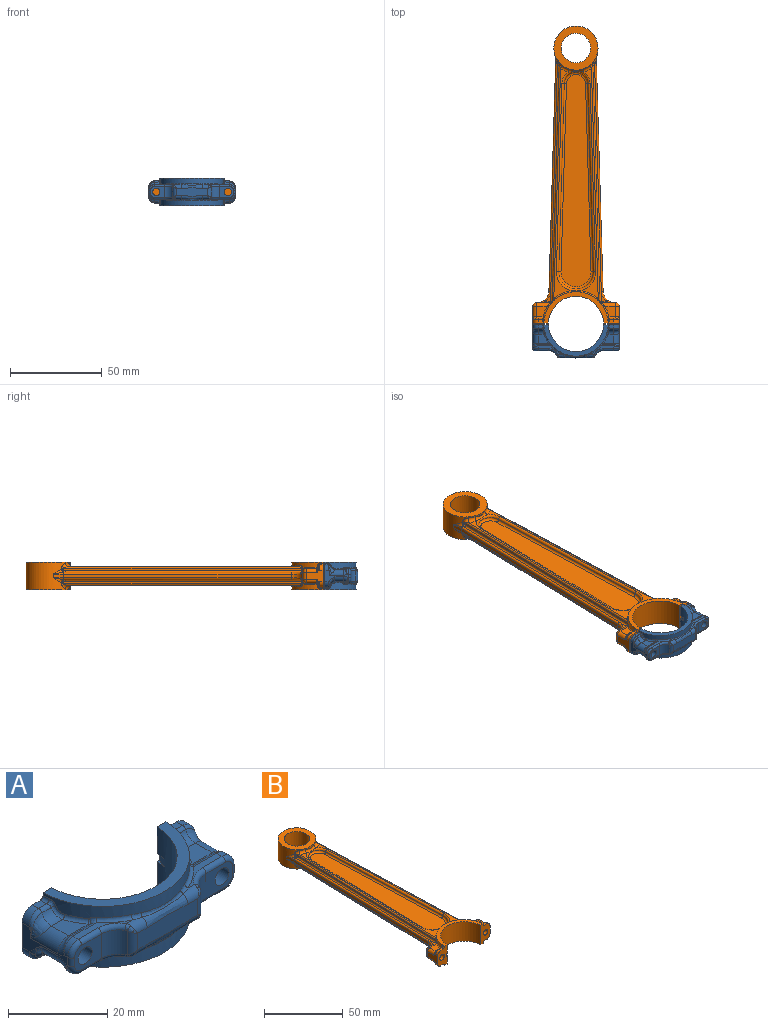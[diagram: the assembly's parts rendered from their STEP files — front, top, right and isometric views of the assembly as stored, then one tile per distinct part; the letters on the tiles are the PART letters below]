
ASSEMBLY  parts=2 mates=1
PART A: 147 faces, bbox 54.2x18.3x15.2 mm
  f0: plane 15.01x8.51mm, normal (0,1,0), area 92.1mm2, adj f1,f27,f28,f29,f30,f38,f39,f40
  f1: cylinder r=15mm len=29.98mm, axis (0,0,-1), area 686.7mm2, adj f0,f36,f38,f39,f144,f145,f146
  f2: plane 12.58x4.23mm, normal (0,0,-1), area 11.7mm2, adj f8,f50,f58,f77,f78,f120
  f3: plane 12.58x4.52mm, normal (0,0,1), area 13.7mm2, adj f16,f54,f61,f66,f67,f137
  f4: cylinder r=3mm len=4.6mm, axis (0,-1,0), area 21.7mm2, adj f5,f19,f21,f92
  f5: torus R=3.9mm, axis (1,0,0), area 8.1mm2, adj f4,f19,f22,f52
  f6: cylinder r=3mm len=3mm, axis (0,-1,0), area 4mm2, adj f19,f23,f52,f70
  f7: torus R=3.9mm, axis (-1,0,0), area 8.1mm2, adj f9,f24,f28,f51
  f8: cylinder r=3mm len=3mm, axis (0,1,0), area 4mm2, adj f2,f28,f51,f79
  f9: cylinder r=3mm len=4.6mm, axis (0,1,0), area 21.7mm2, adj f7,f25,f28,f86
  f10: cylinder r=3mm len=7.69mm, axis (0,-1,0), area 27.1mm2, adj f11,f28,f31,f89,f90
  f11: torus R=3.9mm, axis (-1,0,0), area 5.6mm2, adj f10,f28,f32,f49
  f12: cylinder r=3mm len=3mm, axis (0,-1,0), area 5.7mm2, adj f28,f33,f49,f81
  f13: plane 7.59x6mm, normal (0,-1,0), area 31.3mm2, adj f29,f47,f78,f79,f80,f81,f82
  f14: plane 17.15x4.54mm, normal (0,-1,0), area 71.8mm2, adj f56,f57,f58,f59,f60,f61,f62,f63
  f15: plane 7.59x6mm, normal (0,-1,0), area 31.3mm2, adj f20,f46,f67,f68,f69,f70,f71
  f16: cylinder r=3mm len=3mm, axis (0,1,0), area 5.7mm2, adj f3,f19,f55,f68
  f17: torus R=3.9mm, axis (1,0,0), area 5.6mm2, adj f18,f19,f34,f55
  f18: cylinder r=3mm len=7.69mm, axis (0,1,0), area 27.1mm2, adj f17,f19,f35,f94,f95
  f19: plane 13.22x6.22mm, normal (-1,0,0), area 25.3mm2, adj f4,f5,f6,f16,f17,f18,f36,f44
  f20: cylinder r=2mm len=14mm, axis (0,-1,0), area 175.9mm2, adj f15,f36
  f21: plane 5.58x4.6mm, normal (0,0,-1), area 19.6mm2, adj f4,f22,f91,f113
  f22: cylinder r=0.9mm len=5.64mm, axis (1,0,0), area 5.4mm2, adj f5,f21,f53,f114
  f23: plane 12.58x4.23mm, normal (0,0,-1), area 11.7mm2, adj f6,f53,f62,f71,f72,f116
  f24: cylinder r=0.9mm len=5.64mm, axis (1,0,0), area 5.4mm2, adj f7,f25,f50,f122
  f25: plane 5.58x4.6mm, normal (0,0,-1), area 19.6mm2, adj f9,f24,f87,f123
  f26: plane 2.32x1.63mm, normal (0,0,-1), area 3.7mm2, adj f36,f45,f102,f110
  f27: plane 2.32x1.63mm, normal (0,0,-1), area 3.7mm2, adj f0,f43,f109,f126
  f28: plane 13.22x6.22mm, normal (1,0,0), area 25.3mm2, adj f0,f7,f8,f9,f10,f11,f12,f42
  f29: cylinder r=2mm len=14mm, axis (0,-1,0), area 175.9mm2, adj f0,f13
  f30: plane 2.33x1.75mm, normal (0,0,1), area 3.9mm2, adj f0,f42,f106,f127
  f31: plane 5.64x4.74mm, normal (0,0,1), area 20.2mm2, adj f10,f32,f88,f130
  f32: cylinder r=0.9mm len=5.69mm, axis (-1,0,0), area 3.8mm2, adj f11,f31,f48,f131
  f33: plane 12.58x4.52mm, normal (0,0,1), area 13.7mm2, adj f12,f48,f57,f82,f83,f133
  f34: cylinder r=0.9mm len=5.69mm, axis (-1,0,0), area 3.8mm2, adj f17,f35,f54,f139
  f35: plane 5.64x4.74mm, normal (0,0,1), area 20.2mm2, adj f18,f34,f93,f140
  f36: plane 15.01x8.51mm, normal (0,1,0), area 93.4mm2, adj f1,f19,f20,f26,f37,f38,f39,f40
  f37: plane 2.33x1.75mm, normal (0,0,1), area 3.9mm2, adj f36,f44,f99,f143
  f38: plane 34.99x17mm, normal (0,0,1), area 125.1mm2, adj f0,f1,f36,f40
  f39: plane 34.99x17mm, normal (0,0,-1), area 125.1mm2, adj f0,f1,f36,f41
  f40: cylinder r=17.5mm len=34.99mm, axis (0,0,-1), area 143.5mm2, adj f0,f36,f38,f127,f128,f129,f130,f131
  f41: cylinder r=17.5mm len=34.99mm, axis (0,0,-1), area 151.4mm2, adj f0,f36,f39,f110,f111,f112,f113,f114
  f42: cylinder r=3mm len=3mm, axis (0,1,0), area 9.2mm2, adj f0,f28,f30,f105
  f43: cylinder r=3mm len=3mm, axis (0,-1,0), area 9.2mm2, adj f0,f27,f28,f108
  f44: cylinder r=3mm len=3mm, axis (0,1,0), area 9.2mm2, adj f19,f36,f37,f98
  f45: cylinder r=3mm len=3mm, axis (0,-1,0), area 9.2mm2, adj f19,f26,f36,f101
  f46: cylinder r=5mm len=6mm, axis (0,0,1), area 33.8mm2, adj f15,f63,f65,f66,f72,f73
  f47: cylinder r=5mm len=6mm, axis (0,0,-1), area 33.8mm2, adj f13,f56,f76,f77,f83,f84
  f48: cylinder r=1mm len=6.66mm, axis (-1,0,0), area 4.6mm2, adj f32,f33,f49,f132
  f49: bspline ~3.51x3mm, area 1.4mm2, adj f11,f12,f48
  f50: cylinder r=1mm len=6.92mm, axis (1,0,0), area 6.8mm2, adj f2,f24,f51,f121
  f51: bspline ~3x3mm, area 2mm2, adj f7,f8,f50
  f52: bspline ~3.67x3mm, area 2mm2, adj f5,f6,f53
  f53: cylinder r=1mm len=6.92mm, axis (1,0,0), area 6.8mm2, adj f22,f23,f52,f115
  f54: cylinder r=1mm len=6.66mm, axis (-1,0,0), area 4.6mm2, adj f3,f34,f55,f138
  f55: bspline ~3.51x3mm, area 1.4mm2, adj f16,f17,f54
  f56: cylinder r=2mm len=5.81mm, axis (0,0,-1), area 11.1mm2, adj f14,f47,f75,f85
  f57: cylinder r=2mm len=3.87mm, axis (-1,0,0), area 9.9mm2, adj f14,f33,f59,f84,f85,f134
  f58: cylinder r=2mm len=3.87mm, axis (1,0,0), area 9.9mm2, adj f2,f14,f60,f75,f76,f119
  f59: bspline ~12.87x2.37mm, area 22.9mm2, adj f14,f57,f61,f135
  f60: bspline ~12.87x2.37mm, area 22.9mm2, adj f14,f58,f62,f118
  f61: cylinder r=2mm len=3.87mm, axis (-1,0,0), area 9.9mm2, adj f3,f14,f59,f64,f65,f136
  f62: cylinder r=2mm len=3.87mm, axis (1,0,0), area 9.9mm2, adj f14,f23,f60,f73,f74,f117
  f63: cylinder r=2mm len=5.81mm, axis (0,0,1), area 11.1mm2, adj f14,f46,f64,f74
  f64: bspline ~1.87x1.87mm, area 1.2mm2, adj f61,f63,f65
  f65: bspline ~1.8x1.41mm, area 1mm2, adj f46,f61,f64,f66
  f66: torus R=6mm, axis (0,0,1), area 8.8mm2, adj f3,f46,f65,f67
  f67: cylinder r=1mm len=5.59mm, axis (-1,0,0), area 8.8mm2, adj f3,f15,f66,f68
  f68: torus R=2mm, axis (0,1,0), area 6.5mm2, adj f15,f16,f67,f69
  f69: cylinder r=1mm len=2mm, axis (0,0,-1), area 3.1mm2, adj f15,f19,f68,f70
  f70: torus R=2mm, axis (0,1,0), area 6.5mm2, adj f6,f15,f69,f71
  f71: cylinder r=1mm len=5.59mm, axis (1,0,0), area 8.8mm2, adj f15,f23,f70,f72
  f72: torus R=6mm, axis (0,0,1), area 8.8mm2, adj f23,f46,f71,f73
  f73: bspline ~2.01x1.47mm, area 1mm2, adj f46,f62,f72,f74
  f74: bspline ~1.87x1.87mm, area 1.2mm2, adj f62,f63,f73
  f75: bspline ~1.87x1.87mm, area 1.2mm2, adj f56,f58,f76
  f76: bspline ~1.8x1.41mm, area 1mm2, adj f47,f58,f75,f77
  f77: torus R=6mm, axis (0,0,1), area 8.8mm2, adj f2,f47,f76,f78
  f78: cylinder r=1mm len=5.59mm, axis (1,0,0), area 8.8mm2, adj f2,f13,f77,f79
  f79: torus R=2mm, axis (0,1,0), area 6.5mm2, adj f8,f13,f78,f80
  f80: cylinder r=1mm len=2mm, axis (0,0,-1), area 3.1mm2, adj f13,f28,f79,f81
  f81: torus R=2mm, axis (0,1,0), area 6.5mm2, adj f12,f13,f80,f82
  f82: cylinder r=1mm len=5.59mm, axis (-1,0,0), area 8.8mm2, adj f13,f33,f81,f83
  f83: torus R=6mm, axis (0,0,1), area 8.8mm2, adj f33,f47,f82,f84
  f84: bspline ~2.01x1.47mm, area 1mm2, adj f47,f57,f83,f85
  f85: bspline ~1.87x1.87mm, area 1.2mm2, adj f56,f57,f84
  f86: torus R=6mm, axis (0,-1,0), area 11.5mm2, adj f9,f87,f107,f108
  f87: cylinder r=3mm len=3.2mm, axis (-1,0,0), area 11.5mm2, adj f25,f86,f109,f124
  f88: cylinder r=3mm len=3.19mm, axis (-1,0,0), area 10.3mm2, adj f31,f89,f106,f129
  f89: bspline ~4.43x3.56mm, area 10.6mm2, adj f10,f88,f90,f104,f105
  f90: bspline ~3.15x2.14mm, area 1.2mm2, adj f10,f89,f103
  f91: cylinder r=3mm len=3.2mm, axis (1,0,0), area 11.5mm2, adj f21,f92,f102,f112
  f92: torus R=6mm, axis (0,1,0), area 11.5mm2, adj f4,f91,f100,f101
  f93: cylinder r=3mm len=3.19mm, axis (1,0,0), area 10.3mm2, adj f35,f94,f99,f141
  f94: bspline ~4.44x3.7mm, area 10.6mm2, adj f18,f93,f95,f97,f98
  f95: bspline ~3.15x2.14mm, area 1.2mm2, adj f18,f94,f96
  f96: bspline ~2.53x0.55mm, area 0.4mm2, adj f19,f95,f97
  f97: bspline ~0.67x0.67mm, area 0.2mm2, adj f19,f94,f96,f98
  f98: bspline ~3.39x3.32mm, area 4.5mm2, adj f44,f94,f97,f99
  f99: cylinder r=1mm len=2.62mm, axis (1,0,0), area 2.9mm2, adj f37,f93,f98,f142
  f100: bspline ~3.73x3.37mm, area 1.9mm2, adj f19,f92,f101
  f101: bspline ~3.72x3.37mm, area 5.2mm2, adj f45,f92,f100,f102
  f102: cylinder r=1mm len=2.61mm, axis (1,0,0), area 3.2mm2, adj f26,f91,f101,f111
  f103: bspline ~2.38x0.52mm, area 0.4mm2, adj f28,f90,f104
  f104: bspline ~0.65x0.62mm, area 0.2mm2, adj f28,f89,f103,f105
  f105: bspline ~3.39x3.32mm, area 4.5mm2, adj f42,f89,f104,f106
  f106: cylinder r=1mm len=2.62mm, axis (-1,0,0), area 2.9mm2, adj f30,f88,f105,f128
  f107: bspline ~3.73x3.37mm, area 1.9mm2, adj f28,f86,f108
  f108: bspline ~3.72x3.37mm, area 5.2mm2, adj f43,f86,f107,f109
  f109: cylinder r=1mm len=2.61mm, axis (-1,0,0), area 3.2mm2, adj f27,f87,f108,f125
  f110: torus R=18.3mm, axis (0,0,1), area 2mm2, adj f26,f36,f41,f111
  f111: bspline ~2.11x1.77mm, area 2mm2, adj f41,f102,f110,f112
  f112: bspline ~3.71x2.95mm, area 4.1mm2, adj f41,f91,f111,f113
  f113: torus R=18.3mm, axis (0,0,1), area 6.3mm2, adj f21,f41,f112,f114
  f114: bspline ~1.55x1.48mm, area 1mm2, adj f22,f41,f113,f115
  f115: bspline ~2.39x2.39mm, area 2.6mm2, adj f41,f53,f114,f116
  f116: torus R=18.3mm, axis (0,0,1), area 8.7mm2, adj f23,f41,f115,f117
  f117: bspline ~4.41x1.85mm, area 2.4mm2, adj f41,f62,f116,f118
  f118: bspline ~13.52x1.54mm, area 9.3mm2, adj f41,f60,f117,f119
  f119: bspline ~4.92x2.11mm, area 2.4mm2, adj f41,f58,f118,f120
  f120: torus R=18.3mm, axis (0,0,1), area 8.7mm2, adj f2,f41,f119,f121
  f121: bspline ~2.39x2.39mm, area 2.6mm2, adj f41,f50,f120,f122
  f122: bspline ~1.55x1.48mm, area 1mm2, adj f24,f41,f121,f123
  f123: torus R=18.3mm, axis (0,0,1), area 6.3mm2, adj f25,f41,f122,f124
  f124: bspline ~3.71x2.95mm, area 4.1mm2, adj f41,f87,f123,f125
  f125: bspline ~2.11x1.77mm, area 2mm2, adj f41,f109,f124,f126
  f126: torus R=18.3mm, axis (0,0,1), area 2mm2, adj f0,f27,f41,f125
  f127: torus R=18.3mm, axis (0,0,1), area 2.1mm2, adj f0,f30,f40,f128
  f128: bspline ~2.01x1.48mm, area 1.8mm2, adj f40,f106,f127,f129
  f129: bspline ~3.68x2.66mm, area 3.7mm2, adj f40,f88,f128,f130
  f130: torus R=18.3mm, axis (0,0,1), area 6.5mm2, adj f31,f40,f129,f131
  f131: bspline ~1.35x1.31mm, area 0.6mm2, adj f32,f40,f130,f132
  f132: bspline ~2.17x2.13mm, area 1.8mm2, adj f40,f48,f131,f133
  f133: torus R=18.3mm, axis (0,0,1), area 9.2mm2, adj f33,f40,f132,f134
  f134: bspline ~4.92x2.11mm, area 2.4mm2, adj f40,f57,f133,f135
  f135: bspline ~13.52x1.54mm, area 9.3mm2, adj f40,f59,f134,f136
  f136: bspline ~4.41x1.85mm, area 2.4mm2, adj f40,f61,f135,f137
  f137: torus R=18.3mm, axis (0,0,1), area 9.2mm2, adj f3,f40,f136,f138
  f138: bspline ~2.17x2.13mm, area 1.8mm2, adj f40,f54,f137,f139
  f139: bspline ~1.35x1.31mm, area 0.6mm2, adj f34,f40,f138,f140
  f140: torus R=18.3mm, axis (0,0,1), area 6.5mm2, adj f35,f40,f139,f141
  f141: bspline ~3.68x2.66mm, area 3.7mm2, adj f40,f93,f140,f142
  f142: bspline ~2.08x1.64mm, area 1.8mm2, adj f40,f99,f141,f143
  f143: torus R=18.3mm, axis (0,0,1), area 2.1mm2, adj f36,f37,f40,f142
  f144: plane 2.57x2mm, normal (-0.94,0.34,0), area 5.5mm2, adj f0,f1,f145,f146
  f145: plane 2.57x0.94mm, normal (0,0,1), area 0.7mm2, adj f0,f1,f144
  f146: plane 2.57x0.94mm, normal (0,0,-1), area 0.7mm2, adj f0,f1,f144
PART B: 228 faces, bbox 50.3x161.5x16.2 mm
  f0: cylinder r=15mm len=29.98mm, axis (0,0,-1), area 686.7mm2, adj f1,f18,f19,f41,f225,f226,f227
  f1: plane 15.01x8.51mm, normal (0,-1,0), area 92.1mm2, adj f0,f16,f17,f18,f19,f42,f44,f47
  f2: cylinder r=0.8mm len=1.2mm, axis (0,0,-1), area 0.7mm2, adj f12,f16,f37,f103
  f3: cylinder r=0.8mm len=1.2mm, axis (0,0,-1), area 0.7mm2, adj f11,f16,f38,f108
  f4: cylinder r=0.8mm len=1.2mm, axis (0,0,-1), area 0.7mm2, adj f8,f17,f35,f96
  f5: cylinder r=0.8mm len=1.2mm, axis (0,0,-1), area 0.7mm2, adj f7,f17,f36,f101
  f6: cylinder r=2mm len=7.78mm, axis (-1,0,0), area 18.6mm2, adj f24,f40,f59,f127,f128,f129,f133
  f7: bspline ~0.51x0.32mm, area 0mm2, adj f5,f17,f69,f130
  f8: bspline ~0.51x0.24mm, area 0mm2, adj f4,f17,f68,f162
  f9: cylinder r=2mm len=7.78mm, axis (-1,0,0), area 18.6mm2, adj f26,f43,f64,f159,f160,f161,f163
  f10: cylinder r=2mm len=7.78mm, axis (1,0,0), area 18.6mm2, adj f27,f43,f67,f143,f144,f145,f149
  f11: bspline ~0.51x0.32mm, area 0mm2, adj f3,f16,f71,f146
  f12: bspline ~0.51x0.24mm, area 0mm2, adj f2,f16,f70,f114
  f13: cylinder r=2mm len=7.78mm, axis (1,0,0), area 18.6mm2, adj f25,f40,f62,f111,f112,f113,f115
  f14: plane 125.27x9.35mm, normal (0,0,1), area 160.3mm2, adj f23,f82,f85,f106,f107,f216
  f15: plane 125.27x9.35mm, normal (0,0,-1), area 160.3mm2, adj f22,f76,f79,f99,f100,f203
  f16: cylinder r=17.5mm len=34.99mm, axis (0,0,-1), area 109.5mm2, adj f1,f2,f3,f11,f12,f19,f41,f103
  f17: cylinder r=17.5mm len=34.99mm, axis (0,0,-1), area 109.5mm2, adj f1,f4,f5,f7,f8,f18,f41,f96
  f18: plane 34.99x17mm, normal (0,0,-1), area 125.1mm2, adj f0,f1,f17,f41
  f19: plane 34.99x17mm, normal (0,0,1), area 125.1mm2, adj f0,f1,f16,f41
  f20: plane 125.27x9.35mm, normal (0,0,-1), area 160.3mm2, adj f22,f79,f80,f95,f97,f201
  f21: plane 125.27x9.35mm, normal (0,0,1), area 160.3mm2, adj f23,f81,f82,f102,f104,f218
  f22: torus R=7.67mm, axis (0,0,1), area 36mm2, adj f15,f20,f75,f76,f80,f202
  f23: torus R=7.67mm, axis (0,0,1), area 36mm2, adj f14,f21,f81,f85,f86,f217
  f24: plane 5.85x5.7mm, normal (0,0,-1), area 25.9mm2, adj f6,f58,f135,f136
  f25: plane 5.85x5.7mm, normal (0,0,1), area 25.9mm2, adj f13,f61,f118,f119
  f26: plane 5.85x5.7mm, normal (0,0,-1), area 25.9mm2, adj f9,f63,f166,f167
  f27: plane 5.85x5.7mm, normal (0,0,1), area 25.9mm2, adj f10,f65,f151,f152
  f28: plane 5.6x2.76mm, normal (0,0,1), area 4.4mm2, adj f70,f112,f182
  f29: plane 5.6x2.76mm, normal (0,0,1), area 4.4mm2, adj f71,f144,f192
  f30: plane 5.6x2.76mm, normal (0,0,-1), area 4.4mm2, adj f69,f128,f177
  f31: plane 5.6x2.76mm, normal (0,0,-1), area 4.4mm2, adj f68,f160,f187
  f32: plane 123.76x3.64mm, normal (-1,0.03,0), area 247.6mm2, adj f53,f110,f186,f193
  f33: plane 123.76x3.64mm, normal (1,0.03,0), area 247.6mm2, adj f52,f109,f178,f181
  f34: cylinder r=12mm len=24mm, axis (0,0,-1), area 794.7mm2, adj f88,f89,f109,f110,f195,f196,f199,f200
  f35: plane 129.39x3.8mm, normal (-1,0.03,0), area 155.3mm2, adj f4,f68,f95,f197,f199
  f36: plane 129.39x3.8mm, normal (1,0.03,0), area 155.3mm2, adj f5,f69,f99,f205,f207
  f37: plane 129.39x3.8mm, normal (1,0.03,0), area 155.3mm2, adj f2,f70,f102,f220,f221
  f38: plane 129.39x3.8mm, normal (-1,0.03,0), area 155.3mm2, adj f3,f71,f106,f211,f214
  f39: plane 9x6mm, normal (1,0,0), area 41.5mm2, adj f41,f58,f60,f61,f91,f92,f117,f131
  f40: plane 4x0.25mm, normal (0,1,0), area 1mm2, adj f6,f13,f52,f60
  f41: plane 15.01x8.51mm, normal (0,-1,0), area 93.4mm2, adj f0,f16,f17,f18,f19,f39,f48,f51
  f42: plane 9x6mm, normal (-1,0,0), area 41.5mm2, adj f1,f63,f65,f66,f93,f94,f147,f165
  f43: plane 4x0.25mm, normal (0,1,0), area 1mm2, adj f9,f10,f53,f66
  f44: plane 2.33x1.7mm, normal (0,0,1), area 3.8mm2, adj f1,f94,f155,f158
  f45: plane 3.88x0.41mm, normal (0,1,0), area 1.4mm2, adj f148,f151,f153,f155,f156
  f46: plane 3.88x0.41mm, normal (0,1,0), area 1.4mm2, adj f164,f167,f170,f171,f172
  f47: plane 2.33x1.7mm, normal (0,0,-1), area 3.8mm2, adj f1,f93,f172,f174
  f48: plane 2.33x1.7mm, normal (0,0,1), area 3.8mm2, adj f41,f91,f124,f126
  f49: plane 3.88x0.41mm, normal (0,1,0), area 1.4mm2, adj f116,f119,f122,f123,f124
  f50: plane 3.88x0.41mm, normal (0,1,0), area 1.4mm2, adj f132,f135,f137,f139,f140
  f51: plane 2.33x1.7mm, normal (0,0,-1), area 3.8mm2, adj f41,f92,f139,f142
  f52: cylinder r=6.5mm len=6.5mm, axis (0,0,-1), area 24.3mm2, adj f33,f40,f175,f176,f177,f182,f183,f184
  f53: cylinder r=6.5mm len=6.5mm, axis (0,0,1), area 24.3mm2, adj f32,f43,f187,f188,f189,f190,f191,f192
  f54: plane 4x4mm, normal (0,-1,0), area 12.6mm2, adj f55
  f55: cylinder r=2mm len=9mm, axis (0,-1,0), area 113.1mm2, adj f1,f54
  f56: plane 4x4mm, normal (0,-1,0), area 12.6mm2, adj f57
  f57: cylinder r=2mm len=9mm, axis (0,-1,0), area 113.1mm2, adj f41,f56
  f58: cylinder r=2mm len=5.7mm, axis (0,1,0), area 17.9mm2, adj f24,f39,f59,f132
  f59: sphere r=2mm, area 4mm2, adj f6,f58,f60
  f60: cylinder r=2mm len=4mm, axis (0,0,-1), area 12.6mm2, adj f39,f40,f59,f62
  f61: cylinder r=2mm len=5.7mm, axis (0,-1,0), area 17.9mm2, adj f25,f39,f62,f116
  f62: sphere r=2mm, area 4mm2, adj f13,f60,f61
  f63: cylinder r=2mm len=5.7mm, axis (0,-1,0), area 17.9mm2, adj f26,f42,f64,f164
  f64: sphere r=2mm, area 8.6mm2, adj f9,f63,f66
  f65: cylinder r=2mm len=5.7mm, axis (0,1,0), area 17.9mm2, adj f27,f42,f67,f148
  f66: cylinder r=2mm len=4mm, axis (0,0,-1), area 12.6mm2, adj f42,f43,f64,f67
  f67: sphere r=2mm, area 8.6mm2, adj f10,f65,f66
  f68: cylinder r=1mm len=128.53mm, axis (-0.03,-1,0), area 201.9mm2, adj f8,f31,f35,f161,f186,f197
  f69: cylinder r=1mm len=128.53mm, axis (-0.03,1,0), area 201.9mm2, adj f7,f30,f36,f129,f178,f207
  f70: cylinder r=1mm len=128.53mm, axis (0.03,-1,0), area 201.9mm2, adj f12,f28,f37,f113,f181,f221
  f71: cylinder r=1mm len=128.53mm, axis (0.03,1,0), area 201.9mm2, adj f11,f29,f38,f145,f193,f211
  f72: plane 115.5x16.35mm, normal (0,0,1), area 1511.2mm2, adj f83,f84,f86,f87
  f73: plane 115.5x16.35mm, normal (0,0,-1), area 1511.2mm2, adj f74,f75,f77,f78
  f74: cylinder r=1.25mm len=102.1mm, axis (-0.03,1,0), area 200.5mm2, adj f73,f75,f76,f77
  f75: torus R=5.17mm, axis (0,0,1), area 36.1mm2, adj f22,f73,f74,f78
  f76: cylinder r=1.25mm len=102.1mm, axis (0.03,-1,0), area 200.5mm2, adj f15,f22,f74,f79
  f77: torus R=8.17mm, axis (0,0,1), area 56.4mm2, adj f73,f74,f78,f79
  f78: cylinder r=1.25mm len=102.1mm, axis (-0.03,-1,0), area 200.5mm2, adj f73,f75,f77,f80
  f79: torus R=10.67mm, axis (0,0,1), area 60.8mm2, adj f15,f20,f76,f77,f80,f98
  f80: cylinder r=1.25mm len=102.1mm, axis (0.03,1,0), area 200.5mm2, adj f20,f22,f78,f79
  f81: cylinder r=1.25mm len=102.1mm, axis (0.03,-1,0), area 200.5mm2, adj f21,f23,f82,f83
  f82: torus R=10.67mm, axis (0,0,1), area 60.8mm2, adj f14,f21,f81,f84,f85,f105
  f83: cylinder r=1.25mm len=102.1mm, axis (-0.03,1,0), area 200.5mm2, adj f72,f81,f84,f86
  f84: torus R=8.17mm, axis (0,0,1), area 56.4mm2, adj f72,f82,f83,f87
  f85: cylinder r=1.25mm len=102.1mm, axis (0.03,1,0), area 200.5mm2, adj f14,f23,f82,f87
  f86: torus R=5.17mm, axis (0,0,1), area 36.1mm2, adj f23,f72,f83,f87
  f87: cylinder r=1.25mm len=102.1mm, axis (-0.03,-1,0), area 200.5mm2, adj f72,f84,f85,f86
  f88: plane 24x24mm, normal (0,0,1), area 251.3mm2, adj f34,f90
  f89: plane 24x24mm, normal (0,0,-1), area 251.3mm2, adj f34,f90
  f90: cylinder r=8mm len=16mm, axis (0,0,-1), area 754mm2, adj f88,f89
  f91: cylinder r=3mm len=3mm, axis (0,1,0), area 8.8mm2, adj f39,f41,f48,f120,f122
  f92: cylinder r=3mm len=3mm, axis (0,-1,0), area 8.8mm2, adj f39,f41,f51,f134,f137
  f93: cylinder r=3mm len=3mm, axis (0,-1,0), area 8.8mm2, adj f1,f42,f47,f168,f170
  f94: cylinder r=3mm len=3mm, axis (0,1,0), area 8.8mm2, adj f1,f42,f44,f150,f153
  f95: cylinder r=0.8mm len=129.42mm, axis (-0.03,-1,0), area 160.1mm2, adj f20,f35,f96,f200
  f96: bspline ~2.29x1.87mm, area 2.2mm2, adj f4,f17,f95,f97
  f97: torus R=18.3mm, axis (0,0,1), area 12.8mm2, adj f17,f20,f96,f98
  f98: bspline ~6.46x0.92mm, area 5.9mm2, adj f17,f79,f97,f100
  f99: cylinder r=0.8mm len=129.42mm, axis (-0.03,1,0), area 160.1mm2, adj f15,f36,f101,f204
  f100: torus R=18.3mm, axis (0,0,1), area 12.8mm2, adj f15,f17,f98,f101
  f101: bspline ~2.53x1.97mm, area 2.2mm2, adj f5,f17,f99,f100
  f102: cylinder r=0.8mm len=129.42mm, axis (0.03,-1,0), area 160.1mm2, adj f21,f37,f103,f219
  f103: bspline ~2.29x1.87mm, area 2.2mm2, adj f2,f16,f102,f104
  f104: torus R=18.3mm, axis (0,0,1), area 12.8mm2, adj f16,f21,f103,f105
  f105: bspline ~6.46x0.92mm, area 5.9mm2, adj f16,f82,f104,f107
  f106: cylinder r=0.8mm len=129.42mm, axis (0.03,1,0), area 160.1mm2, adj f14,f38,f108,f215
  f107: torus R=18.3mm, axis (0,0,1), area 12.8mm2, adj f14,f16,f105,f108
  f108: bspline ~2.53x1.97mm, area 2.2mm2, adj f3,f16,f106,f107
  f109: cylinder r=22mm len=5.68mm, axis (0,0,-1), area 11.5mm2, adj f33,f34,f179,f180
  f110: cylinder r=22mm len=5.68mm, axis (0,0,-1), area 11.5mm2, adj f32,f34,f185,f194
  f111: bspline ~3.51x1.02mm, area 0.5mm2, adj f13,f112,f184
  f112: cylinder r=0.8mm len=4.43mm, axis (1,0,0), area 4.1mm2, adj f13,f28,f111,f113,f183
  f113: bspline ~1.22x0.97mm, area 1mm2, adj f13,f70,f112,f114
  f114: sphere r=0.8mm, area 0.1mm2, adj f12,f113,f115
  f115: bspline ~3.27x3.03mm, area 3.3mm2, adj f13,f16,f114,f118
  f116: torus R=2.8mm, axis (0,-1,0), area 2.2mm2, adj f49,f61,f117,f119,f120
  f117: bspline ~1.4x1.01mm, area 0.5mm2, adj f39,f116,f120
  f118: torus R=18.3mm, axis (0,0,1), area 7.5mm2, adj f16,f25,f115,f121
  f119: cylinder r=0.8mm len=3.59mm, axis (1,0,0), area 4.5mm2, adj f25,f49,f116,f121
  f120: bspline ~2.85x1.83mm, area 2.5mm2, adj f91,f116,f117,f122
  f121: sphere r=0.8mm, area 0.9mm2, adj f118,f119,f123
  f122: torus R=2.2mm, axis (0,-1,0), area 2.1mm2, adj f49,f91,f120,f124
  f123: cylinder r=0.8mm len=0.78mm, axis (0,0,-1), area 0.4mm2, adj f16,f49,f121,f125
  f124: cylinder r=0.8mm len=2.59mm, axis (1,0,0), area 3.1mm2, adj f48,f49,f122,f125
  f125: bspline ~1.89x1.87mm, area 2mm2, adj f16,f123,f124,f126
  f126: torus R=18.3mm, axis (0,0,1), area 2.1mm2, adj f16,f41,f48,f125
  f127: bspline ~2.9x0.57mm, area 0.5mm2, adj f6,f128,f175
  f128: cylinder r=0.8mm len=4.43mm, axis (-1,0,0), area 4.1mm2, adj f6,f30,f127,f129,f176
  f129: bspline ~1.15x1.06mm, area 1mm2, adj f6,f69,f128,f130
  f130: sphere r=0.8mm, area 0.1mm2, adj f7,f129,f133
  f131: bspline ~1.88x1.36mm, area 0.5mm2, adj f39,f132,f134
  f132: torus R=2.8mm, axis (0,-1,0), area 2.2mm2, adj f50,f58,f131,f134,f135
  f133: bspline ~3.27x3.03mm, area 3.3mm2, adj f6,f17,f130,f136
  f134: bspline ~3.08x2.13mm, area 2.5mm2, adj f92,f131,f132,f137
  f135: cylinder r=0.8mm len=3.59mm, axis (-1,0,0), area 4.5mm2, adj f24,f50,f132,f138
  f136: torus R=18.3mm, axis (0,0,1), area 7.5mm2, adj f17,f24,f133,f138
  f137: torus R=2.2mm, axis (0,-1,0), area 2.1mm2, adj f50,f92,f134,f139
  f138: sphere r=0.8mm, area 0.9mm2, adj f135,f136,f140
  f139: cylinder r=0.8mm len=2.59mm, axis (-1,0,0), area 3.1mm2, adj f50,f51,f137,f141
  f140: cylinder r=0.8mm len=0.78mm, axis (0,0,-1), area 0.4mm2, adj f17,f50,f138,f141
  f141: bspline ~1.95x1.78mm, area 2mm2, adj f17,f139,f140,f142
  f142: torus R=18.3mm, axis (0,0,1), area 2.1mm2, adj f17,f41,f51,f141
  f143: bspline ~2.9x0.57mm, area 0.5mm2, adj f10,f144,f190
  f144: cylinder r=0.8mm len=4.43mm, axis (1,0,0), area 4.1mm2, adj f10,f29,f143,f145,f191
  f145: bspline ~1.15x1.06mm, area 1mm2, adj f10,f71,f144,f146
  f146: sphere r=0.8mm, area 0.1mm2, adj f11,f145,f149
  f147: bspline ~1.88x1.36mm, area 0.5mm2, adj f42,f148,f150
  f148: torus R=2.8mm, axis (0,-1,0), area 2.2mm2, adj f45,f65,f147,f150,f151
  f149: bspline ~3.27x3.03mm, area 3.3mm2, adj f10,f16,f146,f152
  f150: bspline ~3.08x2.13mm, area 2.5mm2, adj f94,f147,f148,f153
  f151: cylinder r=0.8mm len=3.59mm, axis (1,0,0), area 4.5mm2, adj f27,f45,f148,f154
  f152: torus R=18.3mm, axis (0,0,1), area 7.5mm2, adj f16,f27,f149,f154
  f153: torus R=2.2mm, axis (0,-1,0), area 2.1mm2, adj f45,f94,f150,f155
  f154: sphere r=0.8mm, area 0.9mm2, adj f151,f152,f156
  f155: cylinder r=0.8mm len=2.59mm, axis (1,0,0), area 3.1mm2, adj f44,f45,f153,f157
  f156: cylinder r=0.8mm len=0.78mm, axis (0,0,-1), area 0.4mm2, adj f16,f45,f154,f157
  f157: bspline ~1.95x1.78mm, area 2mm2, adj f16,f155,f156,f158
  f158: torus R=18.3mm, axis (0,0,1), area 2.1mm2, adj f1,f16,f44,f157
  f159: bspline ~3.51x1.02mm, area 0.5mm2, adj f9,f160,f189
  f160: cylinder r=0.8mm len=4.43mm, axis (-1,0,0), area 4.1mm2, adj f9,f31,f159,f161,f188
  f161: bspline ~1.22x0.97mm, area 1mm2, adj f9,f68,f160,f162
  f162: sphere r=0.8mm, area 0.1mm2, adj f8,f161,f163
  f163: bspline ~3.27x3.03mm, area 3.3mm2, adj f9,f17,f162,f166
  f164: torus R=2.8mm, axis (0,-1,0), area 2.2mm2, adj f46,f63,f165,f167,f168
  f165: bspline ~1.4x1.01mm, area 0.5mm2, adj f42,f164,f168
  f166: torus R=18.3mm, axis (0,0,1), area 7.5mm2, adj f17,f26,f163,f169
  f167: cylinder r=0.8mm len=3.59mm, axis (-1,0,0), area 4.5mm2, adj f26,f46,f164,f169
  f168: bspline ~2.85x1.83mm, area 2.5mm2, adj f93,f164,f165,f170
  f169: sphere r=0.8mm, area 1.2mm2, adj f166,f167,f171
  f170: torus R=2.2mm, axis (0,-1,0), area 2.1mm2, adj f46,f93,f168,f172
  f171: cylinder r=0.8mm len=0.78mm, axis (0,0,-1), area 0.4mm2, adj f17,f46,f169,f173
  f172: cylinder r=0.8mm len=2.59mm, axis (-1,0,0), area 3.1mm2, adj f46,f47,f170,f173
  f173: bspline ~1.89x1.87mm, area 2mm2, adj f17,f171,f172,f174
  f174: torus R=18.3mm, axis (0,0,1), area 2.1mm2, adj f1,f17,f47,f173
  f175: bspline ~3.23x0.92mm, area 0.9mm2, adj f52,f127,f176
  f176: bspline ~3.26x1.72mm, area 2.3mm2, adj f52,f128,f175,f177
  f177: torus R=7.5mm, axis (0,0,1), area 9.3mm2, adj f30,f52,f176,f178
  f178: cylinder r=1mm len=123.79mm, axis (-0.03,1,0), area 194.4mm2, adj f33,f69,f177,f179,f208
  f179: torus R=23mm, axis (0,0,1), area 3.7mm2, adj f109,f178,f209
  f180: torus R=23mm, axis (0,0,1), area 3.7mm2, adj f109,f181,f224
  f181: cylinder r=1mm len=123.79mm, axis (0.03,-1,0), area 194.4mm2, adj f33,f70,f180,f182,f223
  f182: torus R=7.5mm, axis (0,0,1), area 9.3mm2, adj f28,f52,f181,f183
  f183: bspline ~3.26x1.72mm, area 2.3mm2, adj f52,f112,f182,f184
  f184: bspline ~3.23x0.93mm, area 0.9mm2, adj f52,f111,f183
  f185: torus R=23mm, axis (0,0,1), area 3.7mm2, adj f110,f186,f195
  f186: cylinder r=1mm len=123.79mm, axis (-0.03,-1,0), area 194.4mm2, adj f32,f68,f185,f187,f196
  f187: torus R=7.5mm, axis (0,0,1), area 9.3mm2, adj f31,f53,f186,f188
  f188: bspline ~3.26x1.72mm, area 2.3mm2, adj f53,f160,f187,f189
  f189: bspline ~3.23x0.93mm, area 0.9mm2, adj f53,f159,f188
  f190: bspline ~3.23x0.92mm, area 0.9mm2, adj f53,f143,f191
  f191: bspline ~3.26x1.72mm, area 2.3mm2, adj f53,f144,f190,f192
  f192: torus R=7.5mm, axis (0,0,1), area 9.3mm2, adj f29,f53,f191,f193
  f193: cylinder r=1mm len=123.79mm, axis (0.03,1,0), area 194.4mm2, adj f32,f71,f192,f194,f212
  f194: torus R=23mm, axis (0,0,1), area 3.7mm2, adj f110,f193,f210
  f195: bspline ~5.95x2.73mm, area 4.4mm2, adj f34,f185,f196
  f196: bspline ~3.13x2.24mm, area 1mm2, adj f34,f186,f195,f197,f198
  f197: bspline ~1.52x1.32mm, area 1.5mm2, adj f35,f68,f196,f198
  f198: bspline ~1.52x1.34mm, area 0.4mm2, adj f196,f197,f199
  f199: cylinder r=1.8mm len=1.16mm, axis (0,0,-1), area 0.9mm2, adj f34,f35,f198,f200
  f200: bspline ~4.11x3.04mm, area 6.4mm2, adj f34,f95,f199,f201
  f201: torus R=13.8mm, axis (0,0,1), area 11.9mm2, adj f20,f34,f200,f202
  f202: bspline ~9.76x2.13mm, area 16.1mm2, adj f22,f34,f201,f203
  f203: torus R=13.8mm, axis (0,0,1), area 11.9mm2, adj f15,f34,f202,f204
  f204: bspline ~4.11x3.04mm, area 6.4mm2, adj f34,f99,f203,f205
  f205: cylinder r=1.8mm len=1.16mm, axis (0,0,-1), area 0.9mm2, adj f34,f36,f204,f206
  f206: bspline ~1.52x1.34mm, area 0.4mm2, adj f205,f207,f208
  f207: bspline ~1.7x1.39mm, area 1.5mm2, adj f36,f69,f206,f208
  f208: bspline ~2.48x1.93mm, area 1mm2, adj f34,f178,f206,f207,f209
  f209: bspline ~5.95x2.73mm, area 4.4mm2, adj f34,f179,f208
  f210: bspline ~5.95x2.73mm, area 4.4mm2, adj f34,f194,f212
  f211: bspline ~1.51x1.31mm, area 1.5mm2, adj f38,f71,f212,f213
  f212: bspline ~3.66x2.37mm, area 1mm2, adj f34,f193,f210,f211,f213
  f213: bspline ~1.52x1.34mm, area 0.4mm2, adj f211,f212,f214
  f214: cylinder r=1.8mm len=1.16mm, axis (0,0,-1), area 0.9mm2, adj f34,f38,f213,f215
  f215: bspline ~4.11x3.04mm, area 6.4mm2, adj f34,f106,f214,f216
  f216: torus R=13.8mm, axis (0,0,1), area 11.9mm2, adj f14,f34,f215,f217
  f217: bspline ~9.76x2.13mm, area 16.1mm2, adj f23,f34,f216,f218
  f218: torus R=13.8mm, axis (0,0,1), area 11.9mm2, adj f21,f34,f217,f219
  f219: bspline ~4.11x3.04mm, area 6.4mm2, adj f34,f102,f218,f220
  f220: cylinder r=1.8mm len=1.16mm, axis (0,0,-1), area 0.9mm2, adj f34,f37,f219,f222
  f221: bspline ~1.64x1.38mm, area 1.5mm2, adj f37,f70,f222,f223
  f222: bspline ~1.52x1.34mm, area 0.4mm2, adj f220,f221,f223
  f223: bspline ~2.48x1.93mm, area 1mm2, adj f34,f181,f221,f222,f224
  f224: bspline ~5.95x2.73mm, area 4.4mm2, adj f34,f180,f223
  f225: plane 2.57x2mm, normal (0.94,-0.34,0), area 5.5mm2, adj f0,f1,f226,f227
  f226: plane 2.57x0.94mm, normal (0,0,1), area 0.7mm2, adj f0,f1,f225
  f227: plane 2.57x0.94mm, normal (0,0,-1), area 0.7mm2, adj f0,f1,f225
PLACE A t=(-70.16,1.08,-2.91)mm
PLACE B t=(-70.16,1.08,-2.91)mm fixed
MATE revolute A.f1 <-> B.f0  axis (0,0,-1) through (-70.16,-148.92,4.59)mm
